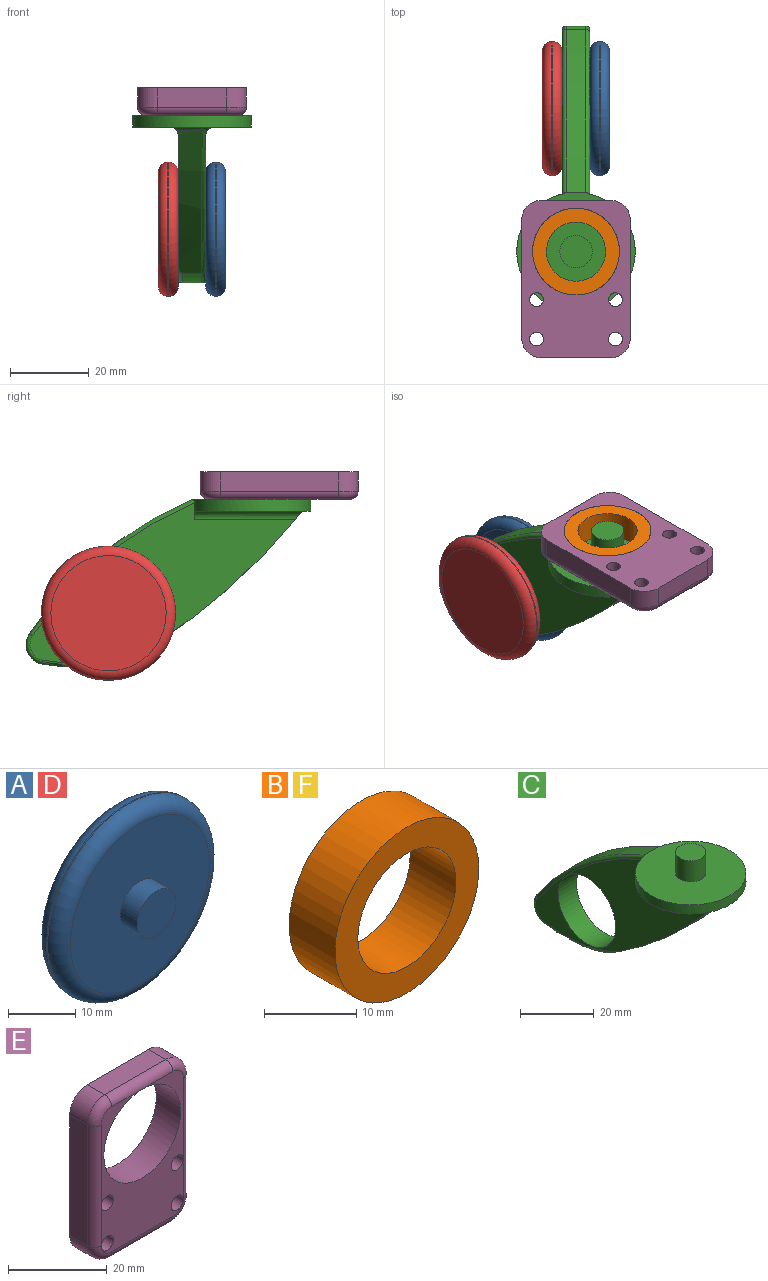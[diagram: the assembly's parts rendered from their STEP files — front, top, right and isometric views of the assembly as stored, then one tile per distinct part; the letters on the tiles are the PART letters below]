
ASSEMBLY  parts=6 mates=5
PART A: 7 faces, bbox 36.8x8.5x36.8 mm
  f0: cylinder r=4.1mm len=8.2mm, axis (0,1,0), area 90.2mm2, adj f1,f4
  f1: plane 8.2x8.2mm, normal (0,-1,0), area 52.8mm2, adj f0
  f2: cylinder r=17mm len=34mm, axis (0,-1,0), area 21.4mm2, adj f5,f6
  f3: plane 29.2x29.2mm, normal (0,1,0), area 669.7mm2, adj f6
  f4: plane 29.2x29.2mm, normal (0,-1,0), area 616.9mm2, adj f0,f5
  f5: torus R=14.6mm, axis (0,-1,0), area 382mm2, adj f2,f4
  f6: torus R=14.6mm, axis (0,-1,0), area 382mm2, adj f2,f3
PART B: 4 faces, bbox 22x7x22 mm
  f0: cylinder r=7.5mm len=15mm, axis (0,1,0), area 329.9mm2, adj f2,f3
  f1: cylinder r=11mm len=22mm, axis (0,1,0), area 483.8mm2, adj f2,f3
  f2: plane 22x22mm, normal (0,-1,0), area 203.4mm2, adj f0,f1
  f3: plane 22x22mm, normal (0,1,0), area 203.4mm2, adj f0,f1
PART C: 23 faces, bbox 30x77.7x53.5 mm
  f0: plane 30x28.96mm, normal (0,0,-1), area 398mm2, adj f8,f19,f20,f21,f22
  f1: plane 30x30mm, normal (0,0,1), area 654.5mm2, adj f5,f8,f9,f12,f17
  f2: cylinder r=152.54mm len=42.09mm, axis (-1,0,0), area 334.2mm2, adj f3,f7,f14,f15,f21,f22
  f3: cylinder r=46.66mm len=23.05mm, axis (-1,0,0), area 116.8mm2, adj f2,f11,f14,f16
  f4: cylinder r=11mm len=22mm, axis (-1,0,0), area 483.8mm2, adj f6,f7
  f5: cylinder r=93.12mm len=41.35mm, axis (-1,0,0), area 271.7mm2, adj f1,f11,f12,f17
  f6: plane 65.96x40.57mm, normal (1,0,0), area 902.6mm2, adj f4,f8,f15,f16,f17,f18,f19
  f7: plane 67.26x40.57mm, normal (-1,0,0), area 953.3mm2, adj f2,f4,f8,f12,f13,f14,f21
  f8: cylinder r=15mm len=30mm, axis (0,0,1), area 263.6mm2, adj f0,f1,f6,f7,f12,f17,f19,f21
  f9: cylinder r=4.1mm len=8.2mm, axis (0,0,-1), area 180.3mm2, adj f1,f10
  f10: plane 8.2x8.2mm, normal (0,0,1), area 52.8mm2, adj f9
  f11: cylinder r=5mm len=7.71mm, axis (-1,0,0), area 49.7mm2, adj f3,f5,f13,f18
  f12: torus R=92.12mm, axis (1,0,0), area 85.3mm2, adj f1,f5,f7,f8,f13
  f13: torus R=4mm, axis (1,0,0), area 14.5mm2, adj f7,f11,f12,f14
  f14: torus R=45.66mm, axis (1,0,0), area 39.7mm2, adj f2,f3,f7,f13
  f15: torus R=151.54mm, axis (1,0,0), area 86.1mm2, adj f2,f6,f16,f20
  f16: torus R=45.66mm, axis (1,0,0), area 36.3mm2, adj f3,f6,f15,f18
  f17: torus R=92.12mm, axis (1,0,0), area 85.3mm2, adj f1,f5,f6,f8,f18
  f18: torus R=4mm, axis (1,0,0), area 14.5mm2, adj f6,f11,f16,f17
  f19: cylinder r=2mm len=24.36mm, axis (0,-1,0), area 75.9mm2, adj f0,f6,f8,f20
  f20: bspline ~4.88x3.56mm, area 9.1mm2, adj f0,f15,f19,f22
  f21: cylinder r=2mm len=28.23mm, axis (0,1,0), area 83.7mm2, adj f0,f2,f7,f8,f22
  f22: cylinder r=2mm len=8mm, axis (-1,0,0), area 12.8mm2, adj f0,f2,f20,f21
PART D: same geometry as A
PART E: 23 faces, bbox 28.3x7x40.7 mm
  f0: plane 17.5x5mm, normal (0,0,-1), area 87.5mm2, adj f1,f11,f14,f15
  f1: cylinder r=5mm len=5mm, axis (0,1,0), area 39.3mm2, adj f0,f2,f14,f17
  f2: plane 29.92x5mm, normal (1,0,0), area 149.6mm2, adj f1,f3,f14,f19
  f3: cylinder r=5mm len=5mm, axis (0,1,0), area 39.3mm2, adj f2,f4,f14,f21
  f4: plane 17.5x5mm, normal (0,0,1), area 87.5mm2, adj f3,f5,f14,f22
  f5: cylinder r=5mm len=5mm, axis (0,1,0), area 39.3mm2, adj f4,f6,f14,f20
  f6: plane 29.92x5mm, normal (-1,0,0), area 149.6mm2, adj f5,f11,f14,f18
  f7: cylinder r=1.75mm len=7mm, axis (0,1,0), area 77mm2, adj f13,f14,f17
  f8: cylinder r=1.75mm len=7mm, axis (0,1,0), area 77mm2, adj f13,f14
  f9: cylinder r=1.75mm len=7mm, axis (0,1,0), area 77mm2, adj f13,f14,f16
  f10: cylinder r=11mm len=22mm, axis (0,1,0), area 483.8mm2, adj f13,f14
  f11: cylinder r=5mm len=5mm, axis (0,1,0), area 39.3mm2, adj f0,f6,f14,f16
  f12: cylinder r=1.75mm len=7mm, axis (0,1,0), area 77mm2, adj f13,f14
  f13: plane 35.92x23.5mm, normal (0,-1,0), area 417.8mm2, adj f7,f8,f9,f10,f12,f15,f16,f17
  f14: plane 39.92x27.5mm, normal (0,1,0), area 657.7mm2, adj f0,f1,f2,f3,f4,f5,f6,f7
  f15: cylinder r=2mm len=17.5mm, axis (-1,0,0), area 55mm2, adj f0,f13,f16,f17
  f16: torus R=3mm, axis (0,-1,0), area 21.1mm2, adj f9,f11,f13,f15,f18
  f17: torus R=3mm, axis (0,-1,0), area 21.1mm2, adj f1,f7,f13,f15,f19
  f18: cylinder r=2mm len=29.92mm, axis (0,0,1), area 94mm2, adj f6,f13,f16,f20
  f19: cylinder r=2mm len=29.92mm, axis (0,0,-1), area 94mm2, adj f2,f13,f17,f21
  f20: torus R=3mm, axis (0,-1,0), area 21.1mm2, adj f5,f13,f18,f22
  f21: torus R=3mm, axis (0,-1,0), area 21.1mm2, adj f3,f13,f19,f22
  f22: cylinder r=2mm len=17.5mm, axis (1,0,0), area 55mm2, adj f4,f13,f20,f21
PART F: same geometry as B
PLACE A rot(axis=(-0.59,-0.59,-0.54),122.9deg) t=(7.54,37.19,-28.98)mm
PLACE B rot(axis=(-1,0,0),90deg) t=(4.04,0.9,-0.12)mm
PLACE C rot(axis=(0,0.06,-1),0deg) t=(0.54,0.9,-0.12)mm
PLACE D rot(axis=(0.56,-0.56,0.61),117.2deg) t=(0.54,37.19,-28.98)mm
PLACE E rot(axis=(0,0.71,0.71),180deg) t=(4.04,0.9,6.88)mm
PLACE F rot(axis=(-0.04,0.04,1),90.1deg) t=(0.54,37.19,-28.98)mm
MATE revolute D.f0 <-> F.f0  axis (1,0,0) through (0.54,37.19,-28.98)mm
MATE revolute A.f0 <-> F.f0  axis (-1,0,0) through (7.54,37.19,-28.98)mm
MATE revolute E.f10 <-> B.f1  axis (0,0,-1) through (4.04,0.9,-0.12)mm
MATE revolute F.f1 <-> C.f4  axis (-1,0,0) through (0.54,37.19,-28.98)mm
MATE revolute B.f0 <-> C.f9  axis (0,0,-1) through (4.04,0.9,-0.12)mm
